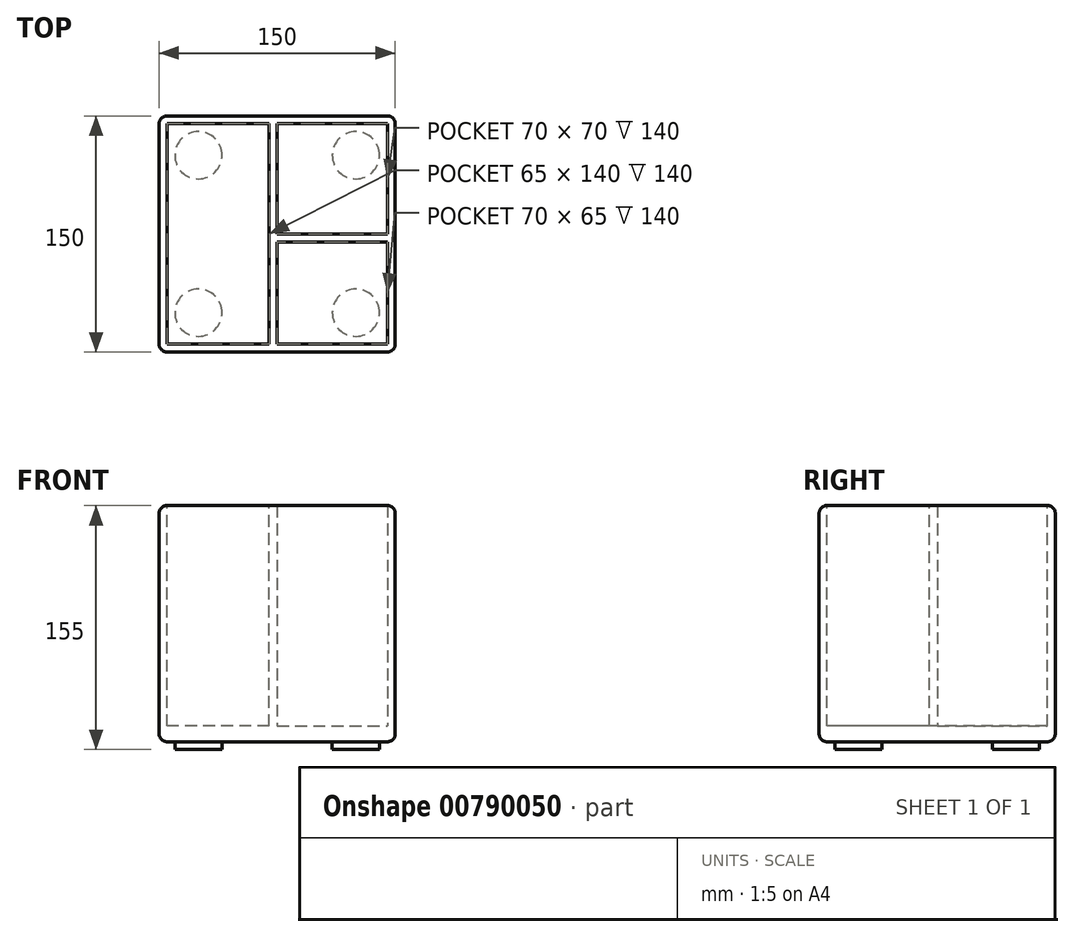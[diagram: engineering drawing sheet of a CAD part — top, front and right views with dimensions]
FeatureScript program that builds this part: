
annotation { "Feature Type Name" : "Feature", "Feature Type Description" : "" }
export const myFeature = defineFeature(function(context is Context, id is Id, definition is map)
    precondition{}
    {
        {
            var Q0;
            Q0=qCreatedBy(makeId("Front.planeOp"),FACE);
            var sketch = newSketch(context, id + "F0", { "sketchPlane" : qUnion([Q0])});
            skLineSegment(sketch, "E0.bottom", {"start": v(75, -75) * mm, "end": v(-75, -75) * mm});
            skLineSegment(sketch, "E0.top", {"start": v(75, 75) * mm, "end": v(-75, 75) * mm});
            skLineSegment(sketch, "E0.left", {"start": v(75, -75) * mm, "end": v(75, 75) * mm});
            skLineSegment(sketch, "E0.right", {"start": v(-75, -75) * mm, "end": v(-75, 75) * mm});
            skPoint(sketch, "E0.middle", {"position": v(0, 0) * mm});
            skSolve(sketch);
        }
        {
            var Q0;
            Q0 = qSketchRegion(id + "F0", true);
            extrude(context, id + "F1", {"entities" : qUnion([Q0]), "endBound" : BoundingType.SYMMETRIC, "depth" : 150 * mm, "offsetDistance" : 25 * mm});
        }
        {
            var Q0;
            Q0=makeQuery(id+"F1.opExtrude","SWEPT_FACE",FACE,{"disambiguationData":[OSD([sQuery(id+"F0.wireOp",EDGE,"E0.top")])]});
            var sketch = newSketch(context, id + "F2", { "sketchPlane" : qUnion([Q0])});
            skLineSegment(sketch, "E1.bottom", {"start": v(70, -70) * mm, "end": v(-70, -70) * mm});
            skLineSegment(sketch, "E1.top", {"start": v(70, 70) * mm, "end": v(-70, 70) * mm});
            skLineSegment(sketch, "E1.left", {"start": v(70, -70) * mm, "end": v(70, 70) * mm});
            skLineSegment(sketch, "E1.right", {"start": v(-70, -70) * mm, "end": v(-70, 70) * mm});
            skPoint(sketch, "E1.middle", {"position": v(0, 0) * mm});
            skSolve(sketch);
        }
        {
            var Q0;
            Q0=makeQuery(id+"F2.imprint","IMPRINT",FACE,{"disambiguationData":[TD([[makeQuery(id+"F2.imprint","IMPRINT",EDGE,{"derivedFrom":sQuery(id+"F2.wireOp",EDGE,"E1.bottom")}),-1.0]])]});
            extrude(context, id + "F3", {"entities" : qUnion([Q0]), "operationType" : NewBodyOperationType.REMOVE, "oppositeDirection" : true, "depth" : 140 * mm, "offsetDistance" : 25 * mm});
        }
        {
            var Q0;
            Q0=makeQuery(id+"F1.opExtrude","CAP_FACE",FACE,{"disambiguationData":[OSD([sQuery(id+"F0.wireOp",EDGE,"E0.bottom"),sQuery(id+"F0.wireOp",EDGE,"E0.top"),sQuery(id+"F0.wireOp",EDGE,"E0.left"),sQuery(id+"F0.wireOp",EDGE,"E0.right")])],"isStart":false});
            var Q1;
            Q1=makeQuery(id+"F1.opExtrude","SWEPT_FACE",FACE,{"disambiguationData":[OSD([sQuery(id+"F0.wireOp",EDGE,"E0.left")])]});
            var Q2;
            Q2=makeQuery(id+"F1.opExtrude","SWEPT_FACE",FACE,{"disambiguationData":[OSD([sQuery(id+"F0.wireOp",EDGE,"E0.right")])]});
            var Q3;
            Q3=makeQuery(id+"F1.opExtrude","CAP_FACE",FACE,{"disambiguationData":[OSD([sQuery(id+"F0.wireOp",EDGE,"E0.bottom"),sQuery(id+"F0.wireOp",EDGE,"E0.top"),sQuery(id+"F0.wireOp",EDGE,"E0.left"),sQuery(id+"F0.wireOp",EDGE,"E0.right")])],"isStart":true});
            var Q4;
            Q4=makeQuery(id+"F1.opExtrude","SWEPT_FACE",FACE,{"disambiguationData":[OSD([sQuery(id+"F0.wireOp",EDGE,"E0.bottom")])]});
            fillet(context, id + "F4", {"entities" : qUnion([Q0, Q1, Q2, Q3, Q4]), "radius" : 5 * mm, "tangentPropagation" : true, "allowEdgeOverflow" : false});
        }
        {
            var Q0;
            Q0=makeQuery(id+"F3.boolean.opBoolean","COPY",FACE,{"derivedFrom":makeQuery(id+"F3.opExtrude","CAP_FACE",FACE,{"disambiguationData":[OSD([sQuery(id+"F2.wireOp",EDGE,"E1.bottom"),sQuery(id+"F2.wireOp",EDGE,"E1.top"),sQuery(id+"F2.wireOp",EDGE,"E1.left"),sQuery(id+"F2.wireOp",EDGE,"E1.right")])],"isStart":false})});
            var sketch = newSketch(context, id + "F5", { "sketchPlane" : qUnion([Q0])});
            skLineSegment(sketch, "E2.bottom", {"start": v(0, -70) * mm, "end": v(-70, -70) * mm});
            skLineSegment(sketch, "E2.top", {"start": v(0, 70) * mm, "end": v(-70, 70) * mm});
            skLineSegment(sketch, "E2.left", {"start": v(0, -70) * mm, "end": v(0, 70) * mm});
            skLineSegment(sketch, "E2.right", {"start": v(-70, -70) * mm, "end": v(-70, 70) * mm});
            skSolve(sketch);
        }
        {
            var Q0;
            Q0=makeQuery(id+"F5.imprint","IMPRINT",FACE,{"disambiguationData":[TD([[makeQuery(id+"F5.imprint","IMPRINT",EDGE,{"derivedFrom":sQuery(id+"F5.wireOp",EDGE,"E2.bottom")}),-1.0]])]});
            extrude(context, id + "F6", {"entities" : qUnion([Q0]), "operationType" : NewBodyOperationType.ADD, "depth" : 140 * mm, "offsetDistance" : 25 * mm});
        }
        {
            var Q0;
            Q0=makeQuery(id+"F6.opExtrude","CAP_FACE",FACE,{"disambiguationData":[OSD([sQuery(id+"F5.wireOp",EDGE,"E2.bottom"),sQuery(id+"F5.wireOp",EDGE,"E2.top"),sQuery(id+"F5.wireOp",EDGE,"E2.left"),sQuery(id+"F5.wireOp",EDGE,"E2.right")])],"isStart":false});
            var sketch = newSketch(context, id + "F7", { "sketchPlane" : qUnion([Q0])});
            skLineSegment(sketch, "E3.bottom", {"start": v(-70, 70) * mm, "end": v(-5, 70) * mm});
            skLineSegment(sketch, "E3.top", {"start": v(-70, -70) * mm, "end": v(-5, -70) * mm});
            skLineSegment(sketch, "E3.left", {"start": v(-70, 70) * mm, "end": v(-70, -70) * mm});
            skLineSegment(sketch, "E3.right", {"start": v(-5, 70) * mm, "end": v(-5, -70) * mm});
            skSolve(sketch);
        }
        {
            var Q0;
            Q0=makeQuery(id+"F7.imprint","IMPRINT",FACE,{"disambiguationData":[TD([[makeQuery(id+"F7.imprint","IMPRINT",EDGE,{"derivedFrom":sQuery(id+"F7.wireOp",EDGE,"E3.bottom")}),1.0]])]});
            extrude(context, id + "F8", {"entities" : qUnion([Q0]), "operationType" : NewBodyOperationType.REMOVE, "oppositeDirection" : true, "depth" : 140 * mm, "offsetDistance" : 25 * mm});
        }
        {
            var Q0;
            Q0=makeQuery(id+"F3.boolean.opBoolean","COPY",FACE,{"derivedFrom":makeQuery(id+"F3.opExtrude","CAP_FACE",FACE,{"disambiguationData":[OSD([sQuery(id+"F2.wireOp",EDGE,"E1.bottom"),sQuery(id+"F2.wireOp",EDGE,"E1.top"),sQuery(id+"F2.wireOp",EDGE,"E1.left"),sQuery(id+"F2.wireOp",EDGE,"E1.right")])],"isStart":false})});
            var sketch = newSketch(context, id + "F9", { "sketchPlane" : qUnion([Q0])});
            skLineSegment(sketch, "E4.bottom", {"start": v(0, 0) * mm, "end": v(70, 0) * mm});
            skLineSegment(sketch, "E4.top", {"start": v(0, -70) * mm, "end": v(70, -70) * mm});
            skLineSegment(sketch, "E4.left", {"start": v(0, 0) * mm, "end": v(0, -70) * mm});
            skLineSegment(sketch, "E4.right", {"start": v(70, 0) * mm, "end": v(70, -70) * mm});
            skSolve(sketch);
        }
        {
            var Q0;
            Q0=makeQuery(id+"F9.imprint","IMPRINT",FACE,{"disambiguationData":[TD([[makeQuery(id+"F9.imprint","IMPRINT",EDGE,{"derivedFrom":sQuery(id+"F9.wireOp",EDGE,"E4.bottom")}),-1.0]])]});
            extrude(context, id + "F10", {"entities" : qUnion([Q0]), "operationType" : NewBodyOperationType.ADD, "depth" : 140 * mm, "offsetDistance" : 25 * mm});
        }
        {
            var Q0;
            Q0=makeQuery(id+"F10.boolean.opBoolean","MERGE",FACE,{"derivedFrom":[makeQuery(id+"F6.opExtrude","CAP_FACE",FACE,{"disambiguationData":[OSD([sQuery(id+"F5.wireOp",EDGE,"E2.bottom"),sQuery(id+"F5.wireOp",EDGE,"E2.top"),sQuery(id+"F5.wireOp",EDGE,"E2.left"),sQuery(id+"F5.wireOp",EDGE,"E2.right")])],"isStart":false}),makeQuery(id+"F10.opExtrude","CAP_FACE",FACE,{"disambiguationData":[OSD([sQuery(id+"F9.wireOp",EDGE,"E4.bottom"),sQuery(id+"F9.wireOp",EDGE,"E4.top"),sQuery(id+"F9.wireOp",EDGE,"E4.left"),sQuery(id+"F9.wireOp",EDGE,"E4.right")])],"isStart":false})]});
            var sketch = newSketch(context, id + "F11", { "sketchPlane" : qUnion([Q0])});
            skLineSegment(sketch, "E5.bottom", {"start": v(0, -5) * mm, "end": v(70, -5) * mm});
            skLineSegment(sketch, "E5.top", {"start": v(0, -70) * mm, "end": v(70, -70) * mm});
            skLineSegment(sketch, "E5.left", {"start": v(0, -5) * mm, "end": v(0, -70) * mm});
            skLineSegment(sketch, "E5.right", {"start": v(70, -5) * mm, "end": v(70, -70) * mm});
            skSolve(sketch);
        }
        {
            var Q0;
            Q0=makeQuery(id+"F11.imprint","IMPRINT",FACE,{"disambiguationData":[TD([[makeQuery(id+"F11.imprint","IMPRINT",EDGE,{"derivedFrom":sQuery(id+"F11.wireOp",EDGE,"E5.bottom")}),-1.0]])]});
            extrude(context, id + "F12", {"entities" : qUnion([Q0]), "operationType" : NewBodyOperationType.REMOVE, "oppositeDirection" : true, "depth" : 140 * mm, "offsetDistance" : 25 * mm});
        }
        {
            var Q0;
            Q0=makeQuery(id+"F1.opExtrude","SWEPT_FACE",FACE,{"disambiguationData":[OSD([sQuery(id+"F0.wireOp",EDGE,"E0.bottom")])]});
            var sketch = newSketch(context, id + "F13", { "sketchPlane" : qUnion([Q0])});
            skCircle(sketch, "E6", {"center": v(-50, 50) * mm, "radius": 15 * mm});
            skCircle(sketch, "E7", {"center": v(50, 50) * mm, "radius": 15 * mm});
            skCircle(sketch, "E8", {"center": v(-50, -50) * mm, "radius": 15 * mm});
            skCircle(sketch, "E9", {"center": v(50, -50) * mm, "radius": 15 * mm});
            skSolve(sketch);
        }
        {
            var Q0;
            Q0=makeQuery(id+"F13.imprint","IMPRINT",FACE,{"disambiguationData":[TD([[makeQuery(id+"F13.imprint","IMPRINT",EDGE,{"derivedFrom":sQuery(id+"F13.wireOp",EDGE,"E6")}),1.0]])]});
            var Q1;
            Q1=makeQuery(id+"F13.imprint","IMPRINT",FACE,{"disambiguationData":[TD([[makeQuery(id+"F13.imprint","IMPRINT",EDGE,{"derivedFrom":sQuery(id+"F13.wireOp",EDGE,"E7")}),1.0]])]});
            var Q2;
            Q2=makeQuery(id+"F13.imprint","IMPRINT",FACE,{"disambiguationData":[TD([[makeQuery(id+"F13.imprint","IMPRINT",EDGE,{"derivedFrom":sQuery(id+"F13.wireOp",EDGE,"E9")}),1.0]])]});
            var Q3;
            Q3=makeQuery(id+"F13.imprint","IMPRINT",FACE,{"disambiguationData":[TD([[makeQuery(id+"F13.imprint","IMPRINT",EDGE,{"derivedFrom":sQuery(id+"F13.wireOp",EDGE,"E8")}),1.0]])]});
            extrude(context, id + "F14", {"entities" : qUnion([Q0, Q1, Q2, Q3]), "operationType" : NewBodyOperationType.ADD, "depth" : 5 * mm, "offsetDistance" : 25 * mm});
        }
    });
